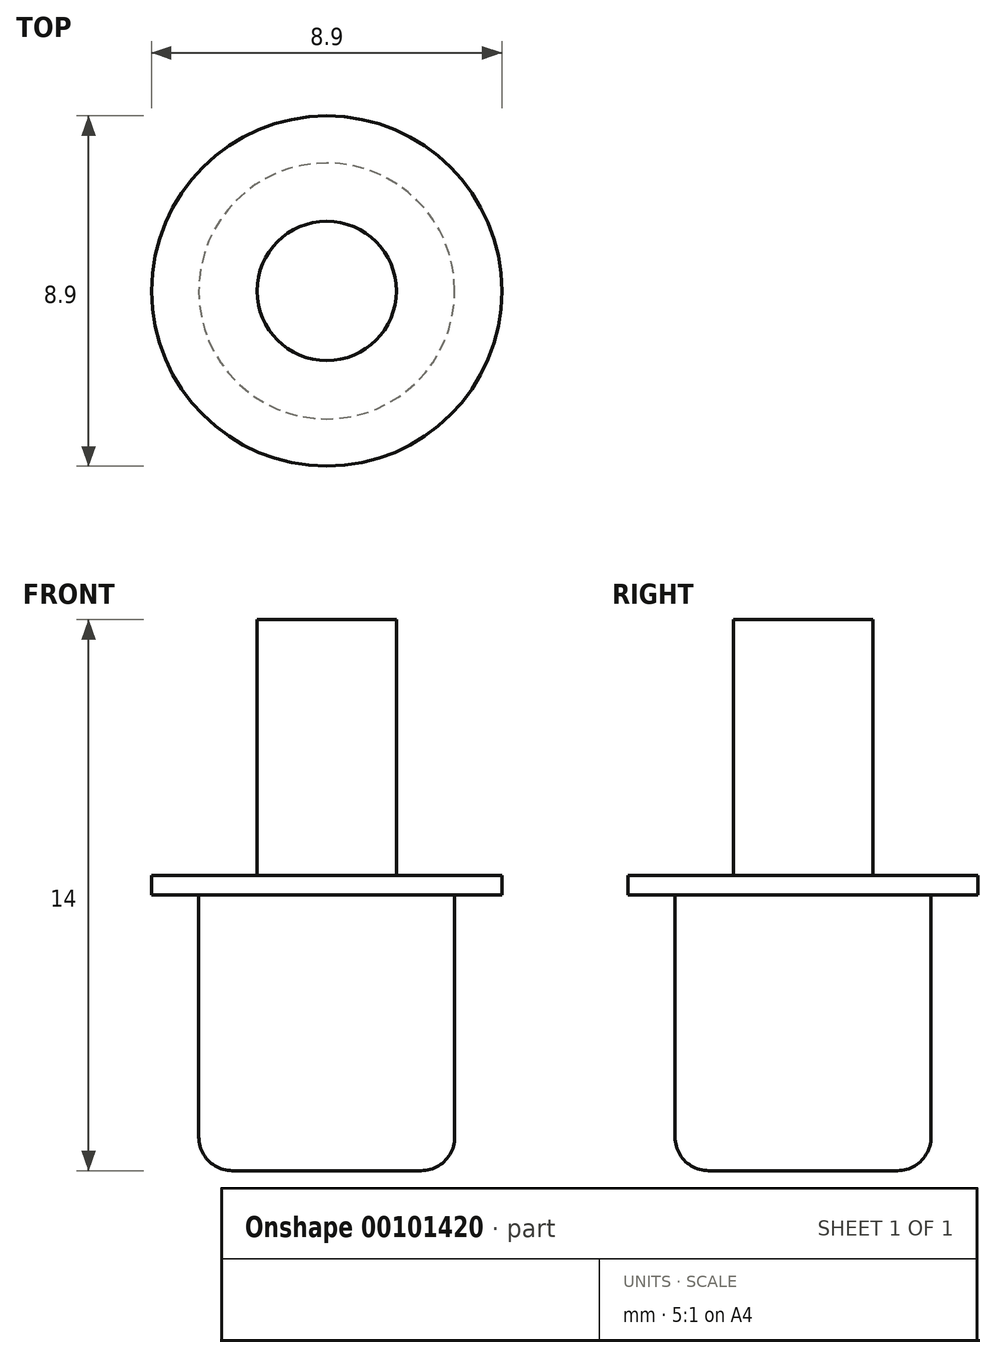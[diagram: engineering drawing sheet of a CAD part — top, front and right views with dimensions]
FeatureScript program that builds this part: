
annotation { "Feature Type Name" : "Feature", "Feature Type Description" : "" }
export const myFeature = defineFeature(function(context is Context, id is Id, definition is map)
    precondition{}
    {
        {
            var Q0;
            Q0=qCreatedBy(makeId("Top.planeOp"),FACE);
            var sketch = newSketch(context, id + "F0", { "sketchPlane" : qUnion([Q0])});
            skCircle(sketch, "E0", {"center": v(0, 0) * mm, "radius": 3.25 * mm});
            skCircle(sketch, "E1", {"center": v(0, 0) * mm, "radius": 1.77 * mm});
            skSolve(sketch);
        }
        {
            var Q0;
            Q0=makeQuery(id+"F0.imprint","IMPRINT",FACE,{"disambiguationData":[TD([[makeQuery(id+"F0.imprint","IMPRINT",EDGE,{"derivedFrom":sQuery(id+"F0.wireOp",EDGE,"E0")}),1.0]])]});
            extrude(context, id + "F1", {"entities" : qUnion([Q0]), "depth" : 7 * mm});
        }
        {
            var Q0;
            Q0=makeQuery(id+"F1.opExtrude","CAP_EDGE",EDGE,{"disambiguationData":[OSD([sQuery(id+"F0.wireOp",EDGE,"E0")])],"isStart":true});
            fillet(context, id + "F2", {"entities" : qUnion([Q0]), "radius" : 0.85 * mm, "tangentPropagation" : true, "allowEdgeOverflow" : false});
        }
        {
            var Q0;
            Q0=makeQuery(id+"F0.imprint","IMPRINT",FACE,{"disambiguationData":[TD([[makeQuery(id+"F0.imprint","IMPRINT",EDGE,{"derivedFrom":sQuery(id+"F0.wireOp",EDGE,"E1")}),1.0]])]});
            extrude(context, id + "F3", {"entities" : qUnion([Q0]), "operationType" : NewBodyOperationType.ADD, "depth" : 14 * mm});
        }
        {
            var Q0;
            Q0=makeQuery(id+"F1.opExtrude","CAP_FACE",FACE,{"disambiguationData":[OSD([sQuery(id+"F0.wireOp",EDGE,"E0"),sQuery(id+"F0.wireOp",EDGE,"E1")])],"isStart":false});
            var sketch = newSketch(context, id + "F4", { "sketchPlane" : qUnion([Q0])});
            skCircle(sketch, "E2", {"center": v(0, 0) * mm, "radius": 4.45 * mm});
            skSolve(sketch);
        }
        {
            var Q0;
            Q0=makeQuery(id+"F4.imprint","IMPRINT",FACE,{"disambiguationData":[TD([[makeQuery(id+"F4.imprint","IMPRINT",EDGE,{"derivedFrom":sQuery(id+"F4.wireOp",EDGE,"E2")}),1.0]])]});
            var Q1;
            Q1=makeQuery(id+"F4.imprint","IMPRINT",FACE,{"disambiguationData":[TD([[makeQuery(id+"F4.imprint","IMPRINT",EDGE,{"derivedFrom":makeQuery(id+"F1.opExtrude","CAP_EDGE",EDGE,{"disambiguationData":[OSD([sQuery(id+"F0.wireOp",EDGE,"E0")])],"isStart":false})}),1.0]])]});
            extrude(context, id + "F5", {"entities" : qUnion([Q0, Q1]), "operationType" : NewBodyOperationType.ADD, "depth" : 0.5 * mm});
        }
    });
